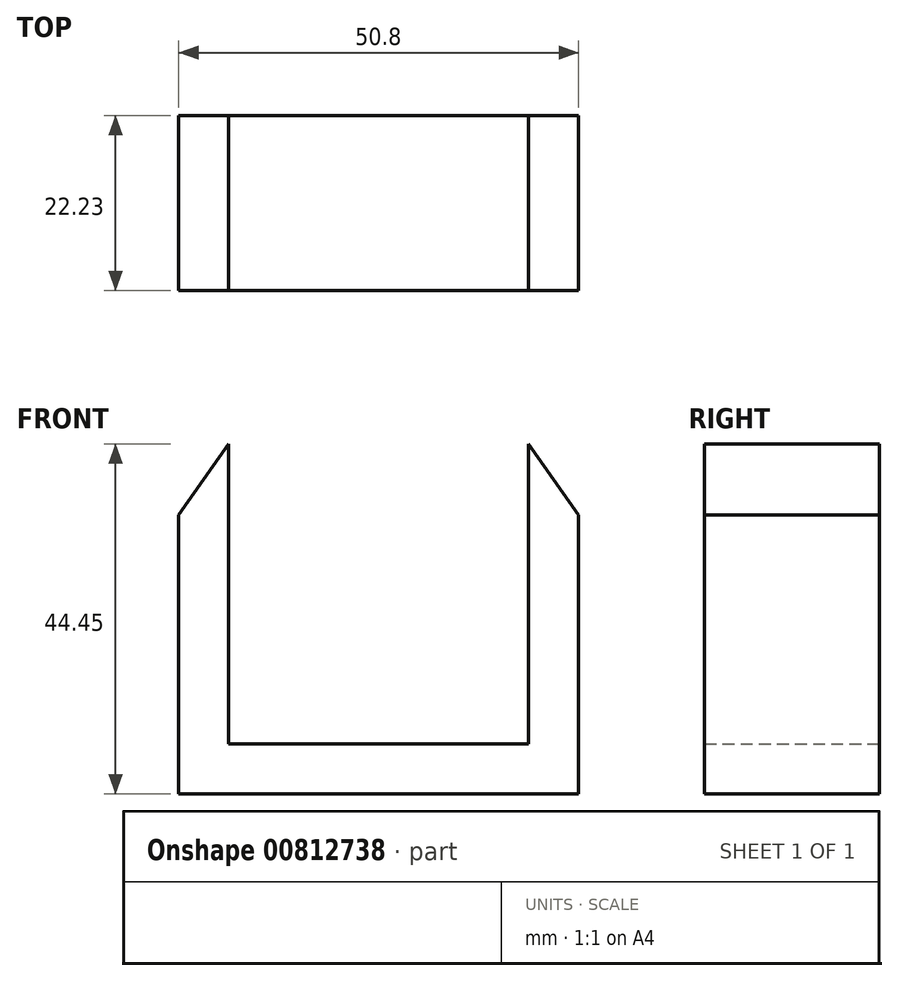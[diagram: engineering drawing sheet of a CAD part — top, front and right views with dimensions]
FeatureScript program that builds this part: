
annotation { "Feature Type Name" : "Feature", "Feature Type Description" : "" }
export const myFeature = defineFeature(function(context is Context, id is Id, definition is map)
    precondition{}
    {
        {
            var Q0;
            Q0=qCreatedBy(makeId("Front.planeOp"),FACE);
            var sketch = newSketch(context, id + "F0", { "sketchPlane" : qUnion([Q0])});
            skLineSegment(sketch, "E0", {"start": v(0, 0) * mm, "end": v(0, -38.1) * mm});
            skLineSegment(sketch, "E1", {"start": v(0, -38.1) * mm, "end": v(38.1, -38.1) * mm});
            skLineSegment(sketch, "E2", {"start": v(38.1, -38.1) * mm, "end": v(38.1, 0) * mm});
            skLineSegment(sketch, "E3", {"start": v(44.45, -9.02) * mm, "end": v(44.45, -44.45) * mm});
            skLineSegment(sketch, "E4", {"start": v(44.45, -44.45) * mm, "end": v(-6.35, -44.45) * mm});
            skLineSegment(sketch, "E5", {"start": v(-6.35, -44.45) * mm, "end": v(-6.35, -9.02) * mm});
            skLineSegment(sketch, "E6", {"start": v(0, 0) * mm, "end": v(-6.35, -9.02) * mm});
            skLineSegment(sketch, "E7", {"start": v(38.1, 0) * mm, "end": v(44.45, -9.02) * mm});
            skPoint(sketch, "E8.orphan", {"position": v(-6.35, 0) * mm});
            skSolve(sketch);
        }
        {
            var Q0;
            Q0 = qSketchRegion(id + "F0", true);
            extrude(context, id + "F1", {"entities" : qUnion([Q0]), "depth" : 22.22 * mm, "offsetDistance" : 25.4 * mm});
        }
    });
